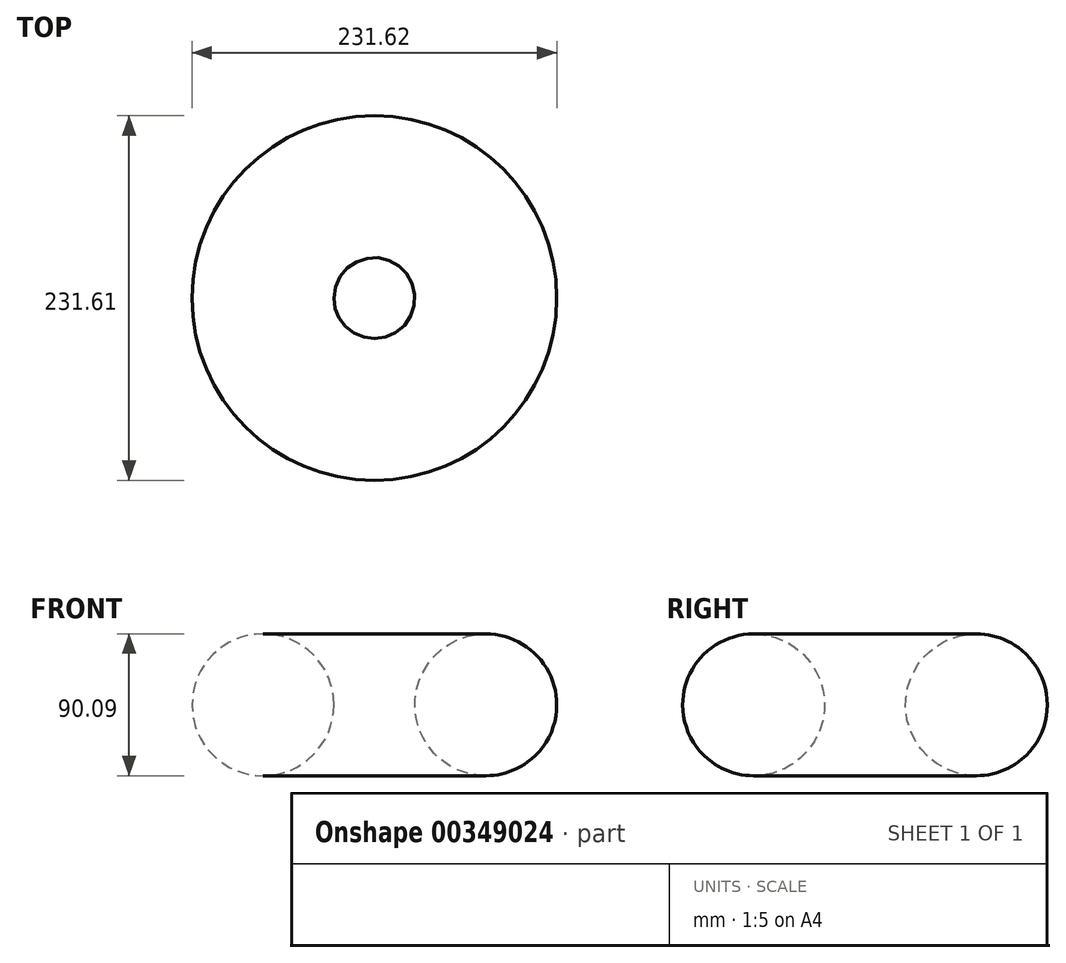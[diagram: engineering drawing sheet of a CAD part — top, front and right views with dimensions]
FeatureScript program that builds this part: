
annotation { "Feature Type Name" : "Feature", "Feature Type Description" : "" }
export const myFeature = defineFeature(function(context is Context, id is Id, definition is map)
    precondition{}
    {
        {
            var Q0;
            Q0=qCreatedBy(makeId("Right.planeOp"),FACE);
            var sketch = newSketch(context, id + "F0", { "sketchPlane" : qUnion([Q0])});
            skLineSegment(sketch, "E0", {"start": v(70.76, -11.92) * mm, "end": v(70.76, 24.13) * mm});
            skSolve(sketch);
        }
        {
            var Q0;
            Q0=qCreatedBy(makeId("Right.planeOp"),FACE);
            var sketch = newSketch(context, id + "F1", { "sketchPlane" : qUnion([Q0])});
            skCircle(sketch, "E1", {"center": v(0, -10.6) * mm, "radius": 45.04 * mm});
            skSolve(sketch);
        }
        {
            var Q0;
            Q0=makeQuery(id+"F1.imprint","IMPRINT",FACE,{"disambiguationData":[TD([[makeQuery(id+"F1.imprint","IMPRINT",EDGE,{"derivedFrom":sQuery(id+"F1.wireOp",EDGE,"E1")}),1.0]])]});
            var Q1;
            Q1=sQuery(id+"F0.wireOp",EDGE,"E0");
            revolve(context, id + "F2", {"entities" : qUnion([Q0]), "axis" : qUnion([Q1]), "revolveType" : RevolveType.FULL});
        }
    });
